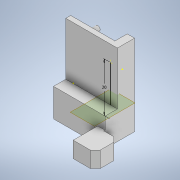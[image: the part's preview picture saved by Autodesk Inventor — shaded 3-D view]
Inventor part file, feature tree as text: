
AUTODESK INVENTOR PART (.ipt)
format: ipt  version: 2021 (Build 250183000, 183)  size: 344,064 bytes
history: native  units: mm
features: sketch x19, extrude x18, other x1, chamfer x1, plane x1, mirror x1
ambient origin geometry x8: Origin, YZ Plane, XZ Plane, XY Plane, X Axis, Y Axis, Z Axis, Center Point
bodies: Body1 (feature_tree)
feature tree (41):
  other  "Sólido1"
  extrude  "Extrusión1"  Depth=9.5mm
  extrude  "Extrusión2"  Depth=14.0mm
  extrude  "Extrusión3"  Depth=2.0mm
  chamfer  "Chaflán1"  Distance=2.0mm
  extrude  "Extrusión4"  Depth=5.0mm
  extrude  "Extrusión5"  Depth=6.0mm
  extrude  "Extrusión6"  Depth=5.0mm
  extrude  "Extrusión7"  Depth=1.25mm
  extrude  "Extrusión8"  Depth=5.0mm
  extrude  "Extrusión9"  Depth=2.0mm TaperAngle=45.0deg
  sketch  "Boceto11"  dims[d19=1.0mm d20=0.0mm d21=2.0mm d22=2.0mm d23=45.0deg]
  plane  "Plano de trabajo1"
  mirror  "Simetría1"
  extrude  "Extrusión10"  Depth=5.0mm
  extrude  "Extrusión11"  Depth=7.5mm
  extrude  "Extrusión12"  Depth=5.0mm
  extrude  "Extrusión13"  Depth=6.0mm
  extrude  "Extrusión14"  Depth=5.0mm
  extrude  "Extrusión15"  Depth=2.5mm
  extrude  "Extrusión16"  Depth=3.0mm TaperAngle=0.0deg
  extrude  "Extrusión17"  Depth=8.0mm TaperAngle=0.0deg
  extrude  "Extrusión18"  Depth=2.0mm
  sketch  "Boceto21"  dims[d46=2.0mm d47=6.0mm d51=6.0mm d52=0.0mm d53=0.5mm d54=0.0mm d55=5.0mm d56=0.0mm d58=20.0mm d59=10.0mm d60=4.0mm d61=0.0mm d62=9.0mm d63=0.0mm d64=6.5mm d65=0.0mm d66=10.0mm d67=2.0mm d68=2.0mm d69=10.0mm d70=2.0mm d71=0.0mm d72=10.0mm d73=10.0mm d74=2.0mm d75=2.0mm d76=6.0mm d77=0.0mm d78=6.0mm d79=0.0mm d80=5.0mm d81=0.0mm d82=10.0mm d83=2.0mm d84=10.0mm d85=2.0mm d86=5.0mm d87=5.0mm d88=0.0mm d89=6.5mm d90=0.0mm]
  sketch  "Boceto1"  dims[d0=4.0mm d1=9.5mm]
  sketch  "Boceto3"  dims[d2=4.0mm d3=0.0mm d4=14.0mm]
  sketch  "Boceto4"  dims[d5=3.0mm d6=20.0mm d7=2.0mm d8=0.0mm]
  sketch  "Boceto5"  dims[d9=5.0mm d10=2.5mm]
  sketch  "Boceto7"  dims[d11=6.0mm d12=6.0mm]
  sketch  "Boceto8"  dims[d13=2.5mm d14=5.0mm]
  sketch  "Boceto9"  dims[d15=2.5mm d16=1.25mm]
  sketch  "Boceto10"  dims[d17=5.0mm d18=2.5mm]
  sketch  "Boceto12"  dims[d25=7.5mm d26=5.0mm]
  sketch  "Boceto13"  dims[d27=20.0mm d28=7.5mm]
  sketch  "Boceto14"  dims[d29=5.0mm d30=2.5mm]
  sketch  "Boceto15"  dims[d31=6.0mm d32=6.0mm]
  sketch  "Boceto16"  dims[d33=5.0mm d34=2.5mm]
  sketch  "Boceto17"  dims[d35=1.25mm d36=2.5mm]
  sketch  "Boceto18"  dims[d37=3.0mm d38=0.0mm d39=2.5mm d40=0.0mm]
  sketch  "Boceto19"  dims[d41=2.0mm d42=8.0mm d43=0.0mm]
  sketch  "Boceto20"  dims[d44=2.0mm d45=4.0mm]
